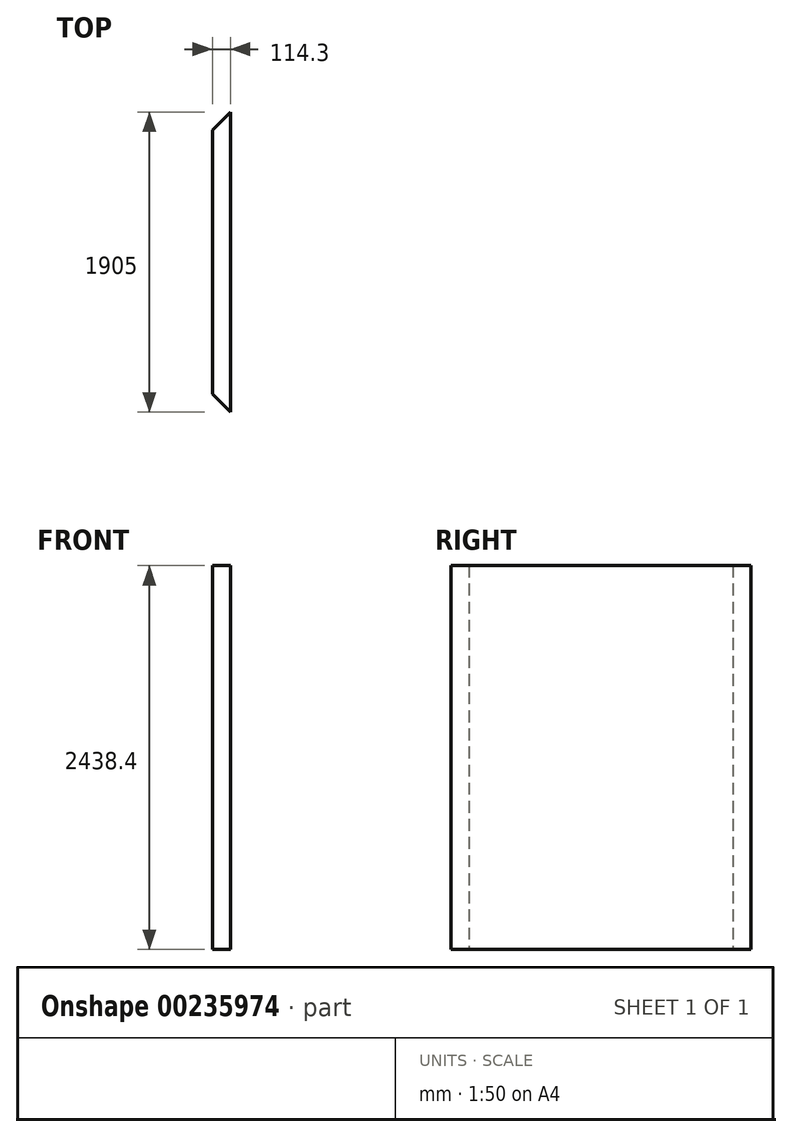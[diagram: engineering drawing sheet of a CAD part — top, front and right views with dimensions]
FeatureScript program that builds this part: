
annotation { "Feature Type Name" : "Feature", "Feature Type Description" : "" }
export const myFeature = defineFeature(function(context is Context, id is Id, definition is map)
    precondition{}
    {
        {
            var Q0;
            Q0=qCreatedBy(makeId("Top.planeOp"),FACE);
            var sketch = newSketch(context, id + "F0", { "sketchPlane" : qUnion([Q0])});
            skLineSegment(sketch, "E0.bottom", {"start": v(57.15, -838.2) * mm, "end": v(-57.15, -838.2) * mm});
            skLineSegment(sketch, "E0.top", {"start": v(57.15, 838.2) * mm, "end": v(-57.15, 838.2) * mm});
            skLineSegment(sketch, "E0.left", {"start": v(57.15, -838.2) * mm, "end": v(57.15, 838.2) * mm});
            skLineSegment(sketch, "E0.right", {"start": v(-57.15, -838.2) * mm, "end": v(-57.15, 838.2) * mm});
            skPoint(sketch, "E0.middle", {"position": v(0, 0) * mm});
            skLineSegment(sketch, "E1", {"start": v(57.15, 838.2) * mm, "end": v(57.15, 952.5) * mm});
            skLineSegment(sketch, "E2", {"start": v(57.15, 952.5) * mm, "end": v(-57.15, 838.2) * mm});
            skLineSegment(sketch, "E3", {"start": v(57.15, -838.2) * mm, "end": v(57.15, -952.5) * mm});
            skLineSegment(sketch, "E4", {"start": v(-57.15, -838.2) * mm, "end": v(57.15, -952.5) * mm});
            skSolve(sketch);
        }
        {
            var Q0;
            Q0 = qSketchRegion(id + "F0", true);
            extrude(context, id + "F1", {"entities" : qUnion([Q0]), "depth" : 2438.4 * mm});
        }
    });
